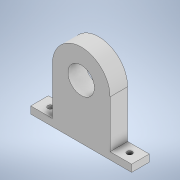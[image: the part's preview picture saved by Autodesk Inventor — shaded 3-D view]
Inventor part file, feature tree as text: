
AUTODESK INVENTOR PART (.ipt)
format: ipt  version: 2021 (Build 250183000, 183)  size: 125,440 bytes
history: native  units: mm
features: extrude x2, sketch x2, other x1
ambient origin geometry x8: Origin, YZ Plane, XZ Plane, XY Plane, X Axis, Y Axis, Z Axis, Center Point
bodies: Body1 (feature_tree)
feature tree (5):
  other  "Sólido1"
  extrude  "Extrusión1"  Depth=7.5mm
  extrude  "Extrusión2"  Depth=5.0mm TaperAngle=0.0deg
  sketch  "Boceto1"  dims[d0=10.0mm d1=0.0mm d2=7.5mm]
  sketch  "Boceto2"  dims[d3=3.0mm d4=5.0mm d5=0.0mm d6=0.15mm d7=0.25mm d8=0.375mm d9=14.3117mm d10=0.75mm d11=20.594885mm d12=0.0625mm d13=0.75mm d14=0.375mm]
